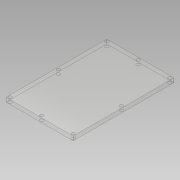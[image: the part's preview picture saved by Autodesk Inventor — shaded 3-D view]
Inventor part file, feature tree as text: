
AUTODESK INVENTOR PART (.ipt)
format: ipt  version: 2019 (Build 230136000, 136)  size: 96,256 bytes
history: native  units: mm
features: sketch x2, other x1, extrude x1, hole x1, projected_geometry x1
ambient origin geometry x8: Origin, YZ Plane, XZ Plane, XY Plane, X Axis, Y Axis, Z Axis, Center Point
bodies: Body1 (feature_tree)
feature tree (6):
  other  "Sólido1"
  extrude  "Extrusión1"  Depth=240.0mm
  hole  "Agujero1"  [1 undecoded]
  sketch  "Boceto1"  dims[d0=160.0mm d1=240.0mm]
  sketch  "Boceto2"  dims[d2=10.0mm d3=0.0mm d4=5.0mm d5=8.0mm d6=6.0mm d7=4.0mm d8=2.0mm d9=90.0deg d10=15.0mm d11=20.594885mm]
  projected_geometry  "Contorno proyectado1"
note: 1 required parameter value undecoded (feature->parameter linkage not recoverable at this tier; creation-order binding heuristic only, values carry confidence <= 0.55)
